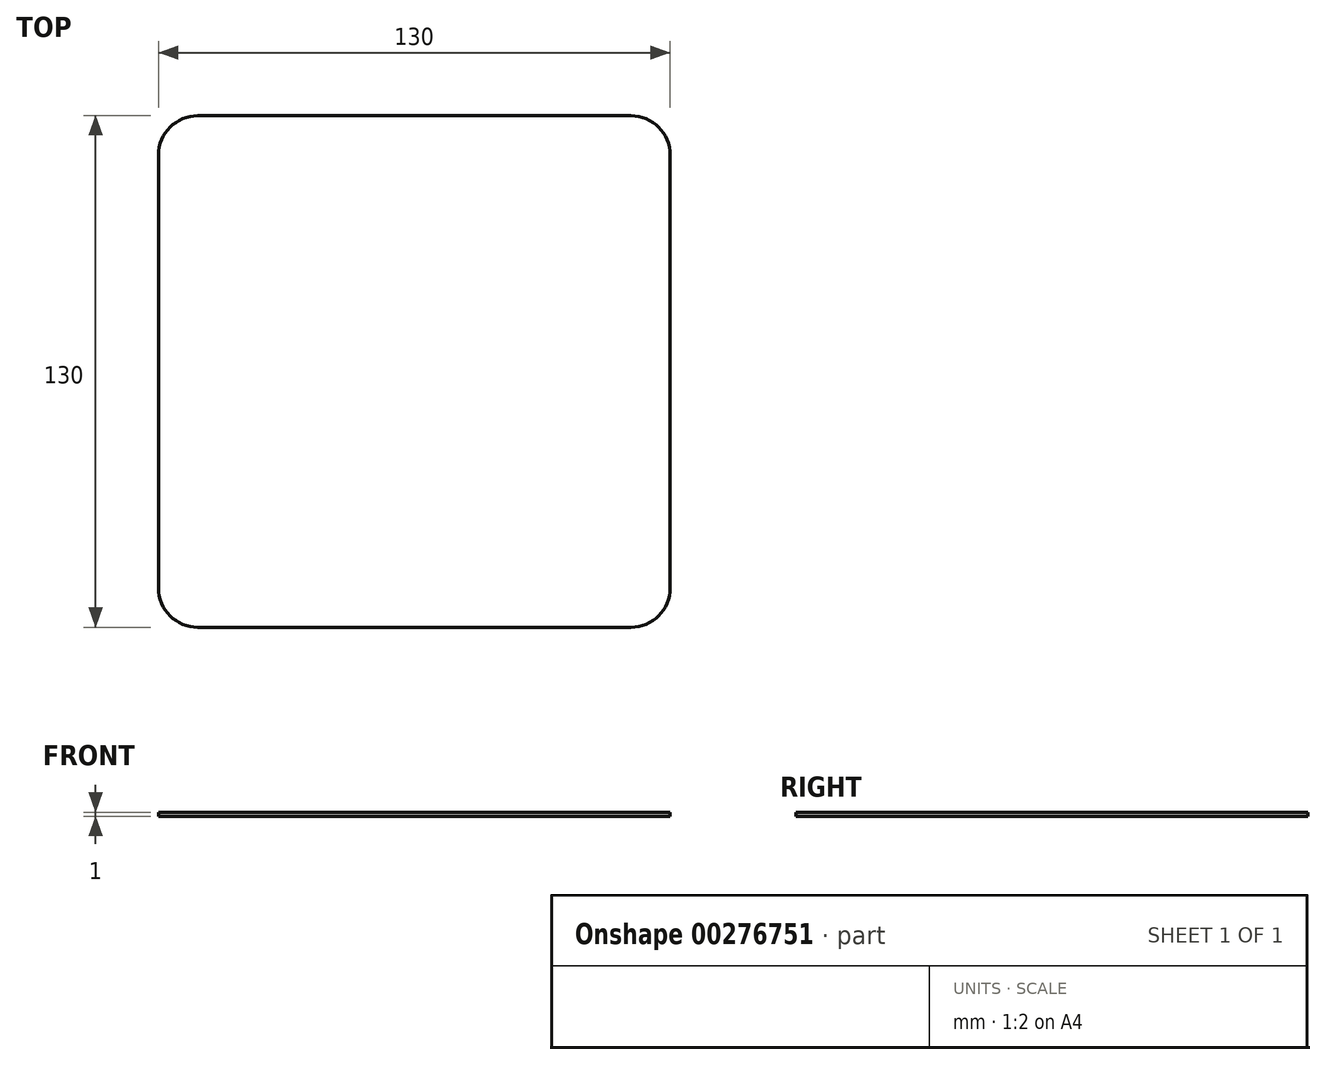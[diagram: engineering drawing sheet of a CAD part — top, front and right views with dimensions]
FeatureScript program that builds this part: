
annotation { "Feature Type Name" : "Feature", "Feature Type Description" : "" }
export const myFeature = defineFeature(function(context is Context, id is Id, definition is map)
    precondition{}
    {
        {
            var Q0;
            Q0=qCreatedBy(makeId("Top.planeOp"),FACE);
            var sketch = newSketch(context, id + "F0", { "sketchPlane" : qUnion([Q0])});
            skLineSegment(sketch, "E0.bottom", {"start": v(-10, 0) * mm, "end": v(-120, 0) * mm});
            skLineSegment(sketch, "E0.top", {"start": v(-10, -130) * mm, "end": v(-120, -130) * mm});
            skLineSegment(sketch, "E0.left", {"start": v(0, -10) * mm, "end": v(0, -120) * mm});
            skLineSegment(sketch, "E0.right", {"start": v(-130, -10) * mm, "end": v(-130, -120) * mm});
            skPoint(sketch, "E1.visualSharp", {"position": v(-130, 0) * mm});
            skArc(sketch, "E1.filletArc", {"start": v(-120, 0) * mm, "mid": v(-127.07, -2.93) * mm, "end": v(-130, -10) * mm});
            skPoint(sketch, "E2.visualSharp", {"position": v(0, 0) * mm});
            skArc(sketch, "E2.filletArc", {"start": v(0, -10) * mm, "mid": v(-2.93, -2.93) * mm, "end": v(-10, 0) * mm});
            skPoint(sketch, "E3.visualSharp", {"position": v(-130, -130) * mm});
            skArc(sketch, "E3.filletArc", {"start": v(-130, -120) * mm, "mid": v(-127.07, -127.07) * mm, "end": v(-120, -130) * mm});
            skPoint(sketch, "E4.visualSharp", {"position": v(0, -130) * mm});
            skArc(sketch, "E4.filletArc", {"start": v(-10, -130) * mm, "mid": v(-2.93, -127.07) * mm, "end": v(0, -120) * mm});
            skSolve(sketch);
        }
        {
            var Q0;
            Q0=makeQuery(id+"F0.imprint","IMPRINT",FACE,{"disambiguationData":[TD([[makeQuery(id+"F0.imprint","IMPRINT",EDGE,{"derivedFrom":sQuery(id+"F0.wireOp",EDGE,"E0.bottom")}),1.0]])]});
            extrude(context, id + "F1", {"entities" : qUnion([Q0]), "depth" : 1 * mm});
        }
    });
